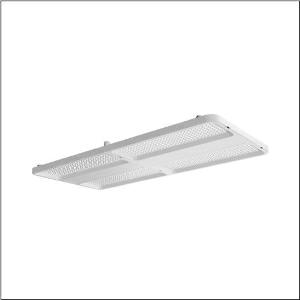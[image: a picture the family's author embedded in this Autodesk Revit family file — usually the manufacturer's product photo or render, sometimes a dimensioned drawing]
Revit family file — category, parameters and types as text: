
# Revit family: highbay_21_maxi_52hn12db6qda
name_source: partatom
category: Lighting Fixtures
units: mm (PartAtom-declared; Revit-internal decimal feet)

## family parameters
Cut with Voids When Loaded = No
Host = Face
Light Source = No
Part Type = Normal
Room Calculation Point = No
Round Connector Dimension = Use Diameter
Shared = No

## types (1)
- --- (1 x LED, 5650 lm, 31.4 W, 6500K)
    Apparent Load = 31 VA
    CIE Flux Codes = 90 98 100 100 100
    Color Rendering = 80
    Color Temperature = 6500K
    Default Elevation = 1800 mm
    Description = high bay luminaire Highbay 21 maxi; direct symmetric wide distribution, light control with lens of PMMA; UGR ≤ 22 (X = 4H | Y = 8H | S = 0.25H | reflection values 70/50/20); luminous flux: 36.840lm; light colour: 865, colour temperature: 6500K, MacAdam ≤ 3 SDCM (initial), colour rendering: CRI > 80; luminous efficacy: 186,3lm/W; rated service life: 75.000h (L80) at AT= ta max; control: DALI 2; luminaire connection: terminal, 5-pole, max. 2.5mm² (cable entry for one cable, Ø 8.5..16mm); mains connection: 230..240V, AC/DC 0/50..60Hz; connected load: 197,7W; protection rating (complete): IP66; insulation class (complete): insulation class I (protective earthing); protection symbol: D; impact resistance: IK08; certification: CE, ENEC, VDE, UKCA; luminaire for central battery installations according to EN 60598-2-22, internal wiring halogen-free; luminaire LABS conformity tested according to VDMA 24364:2018-05; Suitable for use in the food industry according to the specifications of IFS-Food, HACCP and/or BRC; housing frame of high-performance plastic PA6, matt traffic white (RAL 9016); cover of PMMA; dimension (LxWxH): 946 x 442 x 72mm; permissible operating ambient temperature: -40..+60°C (reducing of maximum allowable ambient temperature of 5°C with ceiling mounting); packaging unit: 1 piece; (delivery without accessories; please order mounting accessories separately)
    Height = 72 mm  [stored 0.23622 ft]
    Lamp = 1 x LED
    Lamp Light Flux = 5650 lm
    Lamp Power = 31.4 W
    Lamp count = 1
    Length = 946 mm
    Luminous efficacy = 180 lm/W
    Manufacturer = Siteco
    ModVariant = No
    Model = 52HN12DB6QDA
    Mounting Place = Ceiling
    Mounting Type = Pendant
    Number of Poles = 1
    OnlyDefault = Yes
    Power Factor = 1
    Product Name = Highbay 21 maxi
    Product group = high bay luminaire
    ProductGroupID = 902
    Protection Class = Protection class I
    Protection Degree = IP 66
    RLX_Detail_Level = 1
    RLX_Emergency_Light_Flux = 0 lm
    RLX_Emergency_Type = 0
    RLX_Emergency_Type_DB = No
    RlxData = <blob elided: 128045 chars, md5=0c2439e0>
    Socket = socket
    Standby Power = 0 W
    System Light Flux = 5650 lm
    System Power = 31 W
    Type Comments = : DC mode (central or group accumulator) initial emergency light level
    Type Image = l_1363244.jpg
    URL = http://relux.com
    VarID = @adj_004879
    Voltage = 0 V
    Weight = 0.00 kg
    Width = 442 mm

note: [stored X ft] marks values corroborated as IEEE doubles in the binary element streams (Revit-internal decimal feet)

## geometry (parser evidence)
native form markers: Blend x4, Sweep x10
no freeform markers — native parametric forms only
